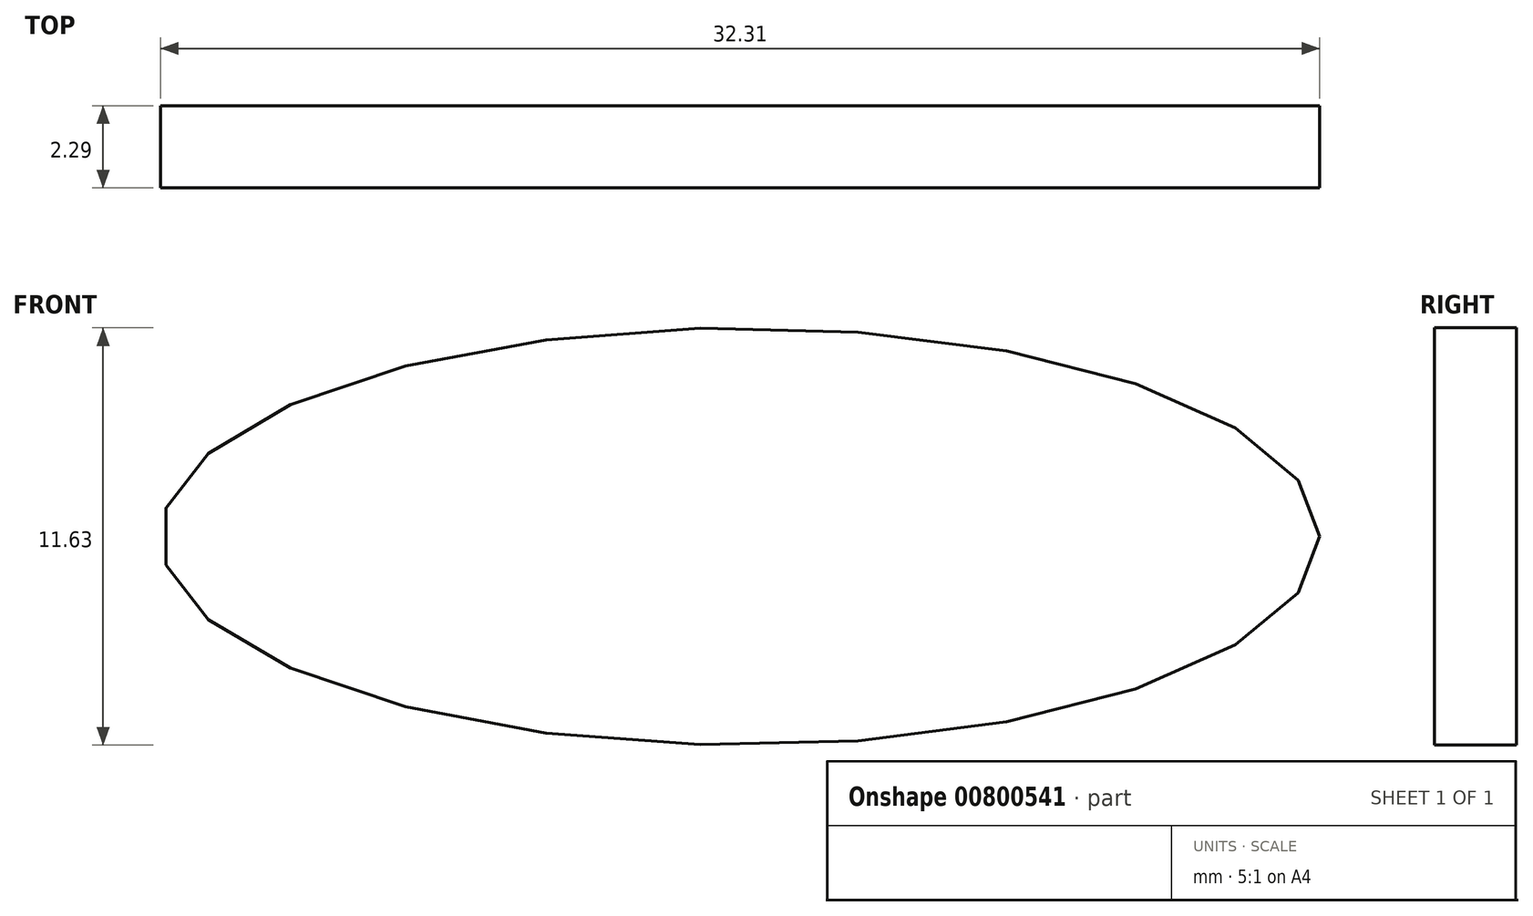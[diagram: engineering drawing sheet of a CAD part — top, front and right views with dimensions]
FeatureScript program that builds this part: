
annotation { "Feature Type Name" : "Feature", "Feature Type Description" : "" }
export const myFeature = defineFeature(function(context is Context, id is Id, definition is map)
    precondition{}
    {
        {
            var Q0;
            Q0=qCreatedBy(makeId("Front.planeOp"),FACE);
            var sketch = newSketch(context, id + "F0", { "sketchPlane" : qUnion([Q0])});
            skEllipse(sketch, "E0", {"center": v(-43.97, 26.75) * mm, "majorRadius": 16.15 * mm, "minorRadius": 5.82 * mm, "majorAxis": v(1, 0)});
            skSolve(sketch);
        }
        {
            var Q0;
            Q0=makeQuery(id+"F0.imprint","IMPRINT",FACE,{"disambiguationData":[TD([[makeQuery(id+"F0.imprint","IMPRINT",EDGE,{"derivedFrom":sQuery(id+"F0.wireOp",EDGE,"E0")}),1.0]])]});
            extrude(context, id + "F1", {"entities" : qUnion([Q0]), "oppositeDirection" : true, "depth" : 2.3 * mm, "offsetDistance" : 25.4 * mm});
        }
    });
